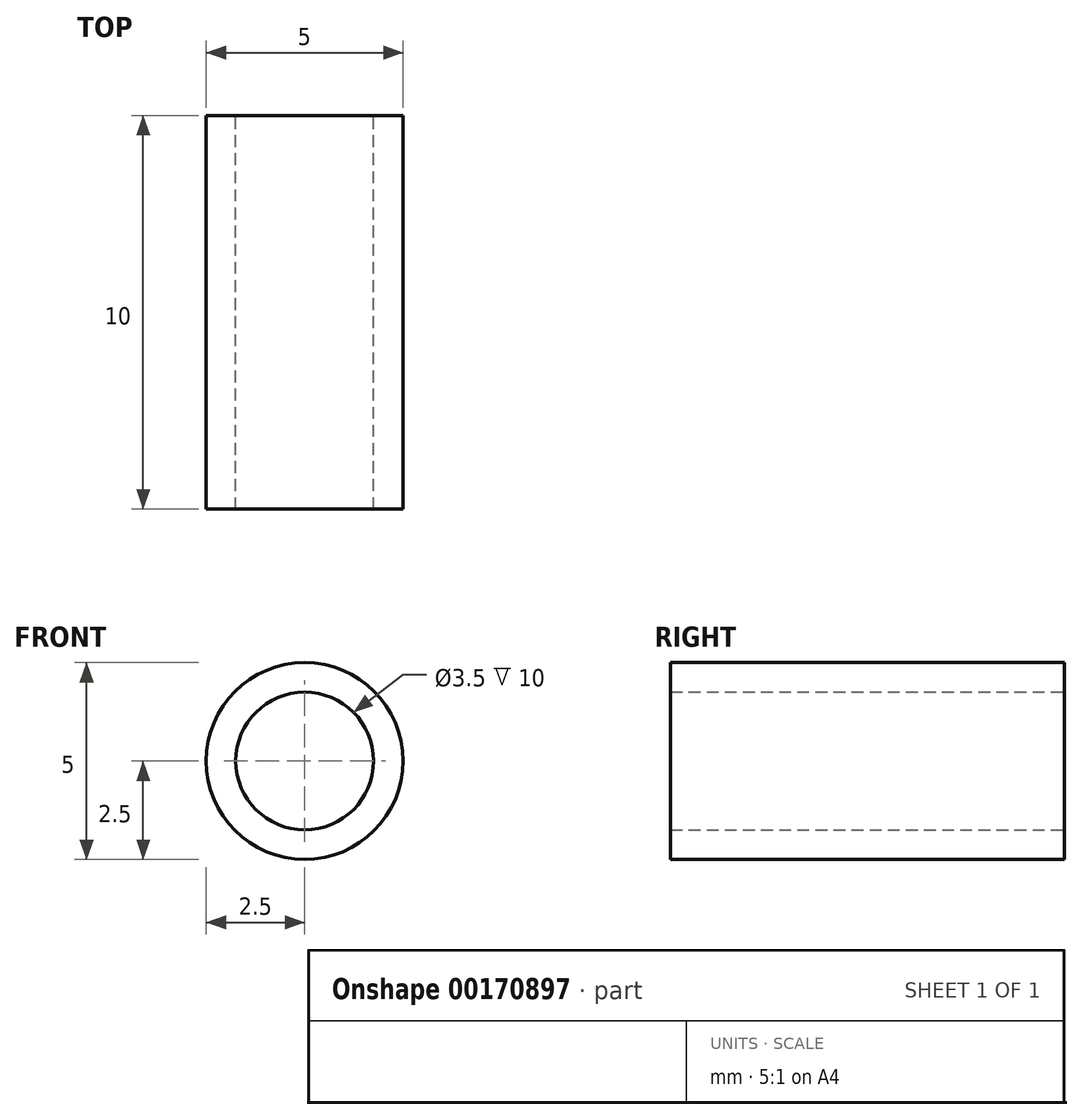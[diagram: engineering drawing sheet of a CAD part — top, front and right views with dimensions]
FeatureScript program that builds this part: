
annotation { "Feature Type Name" : "Feature", "Feature Type Description" : "" }
export const myFeature = defineFeature(function(context is Context, id is Id, definition is map)
    precondition{}
    {
        {
            assignVariable(context, id + "F0", {"name" : "Main_Length", "anyValue" : 10});
        }
        {
            var Q0;
            Q0=qCreatedBy(makeId("Front.planeOp"),FACE);
            var sketch = newSketch(context, id + "F1", { "sketchPlane" : qUnion([Q0])});
            skCircle(sketch, "E0", {"center": v(0, 0) * mm, "radius": 1.75 * mm});
            skCircle(sketch, "E1", {"center": v(0, 0) * mm, "radius": 2.5 * mm});
            skSolve(sketch);
        }
        {
            var Q0;
            Q0=makeQuery(id+"F1.imprint","IMPRINT",FACE,{"disambiguationData":[TD([[makeQuery(id+"F1.imprint","IMPRINT",EDGE,{"derivedFrom":sQuery(id+"F1.wireOp",EDGE,"E0")}),-1.0]])]});
            extrude(context, id + "F2", {"entities" : qUnion([Q0]), "depth" : (getVariable(context, 'Main_Length')) * mm});
        }
    });
